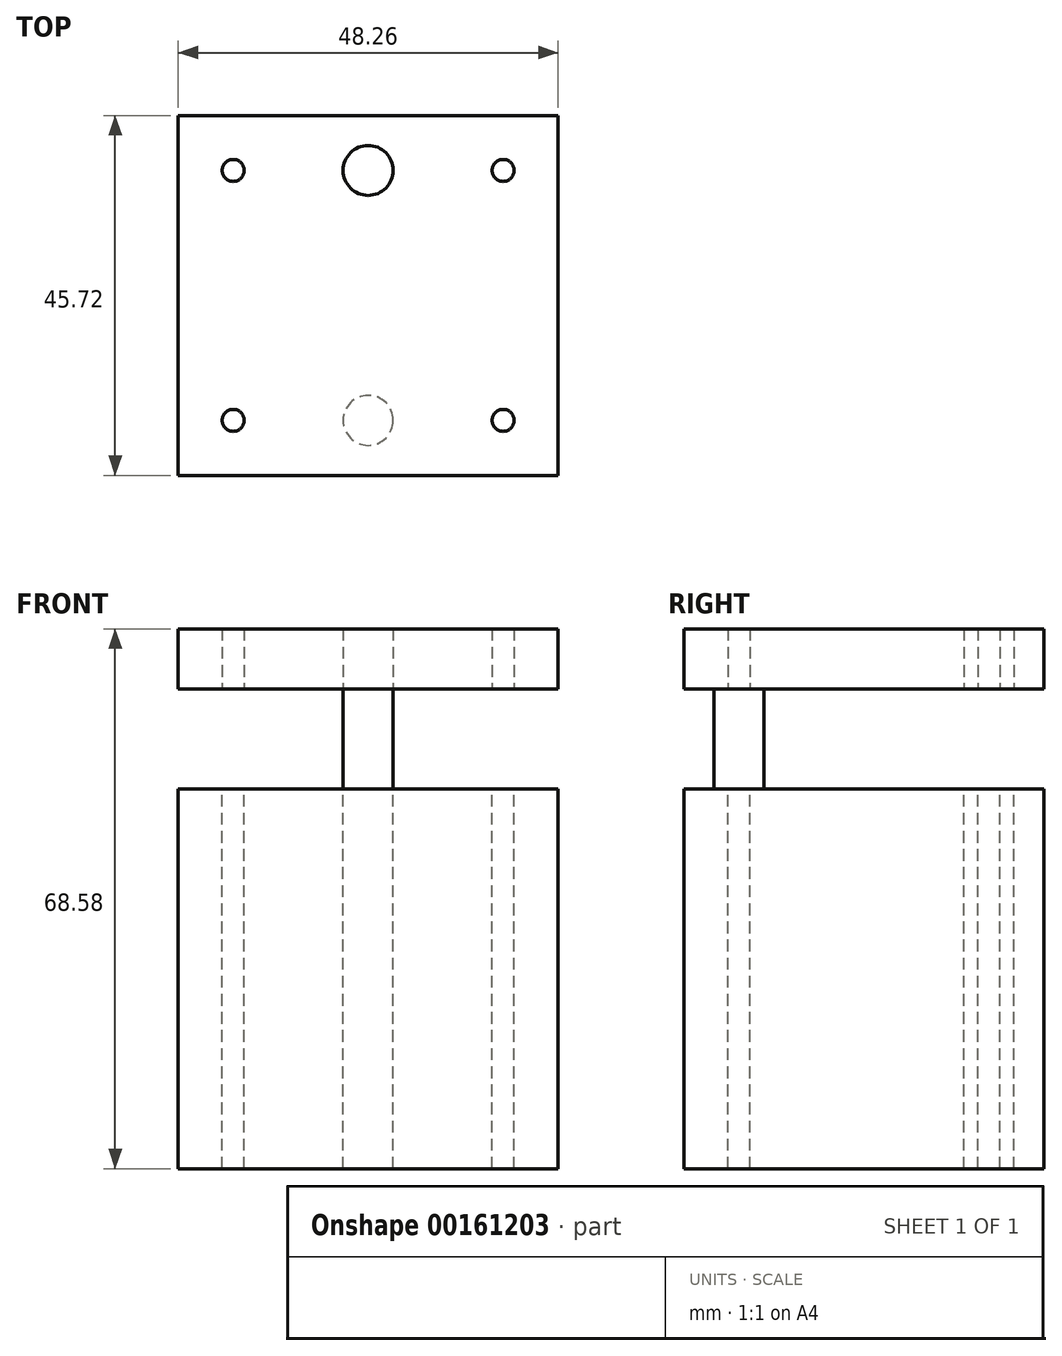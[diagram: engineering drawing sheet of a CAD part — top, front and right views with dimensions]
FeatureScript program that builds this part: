
annotation { "Feature Type Name" : "Feature", "Feature Type Description" : "" }
export const myFeature = defineFeature(function(context is Context, id is Id, definition is map)
    precondition{}
    {
        {
            var Q0;
            Q0=qCreatedBy(makeId("Top.planeOp"),FACE);
            var sketch = newSketch(context, id + "F0", { "sketchPlane" : qUnion([Q0])});
            skLineSegment(sketch, "E0.bottom", {"start": v(24.13, 22.86) * mm, "end": v(-24.13, 22.86) * mm});
            skLineSegment(sketch, "E0.top", {"start": v(24.13, -22.86) * mm, "end": v(-24.13, -22.86) * mm});
            skLineSegment(sketch, "E0.left", {"start": v(24.13, 22.86) * mm, "end": v(24.13, -22.86) * mm});
            skLineSegment(sketch, "E0.right", {"start": v(-24.13, 22.86) * mm, "end": v(-24.13, -22.86) * mm});
            skPoint(sketch, "E0.middle", {"position": v(0, 0) * mm});
            skCircle(sketch, "E1", {"center": v(17.14, -15.87) * mm, "radius": 1.4 * mm});
            skCircle(sketch, "E2.MirrorC", {"center": v(-17.14, -15.87) * mm, "radius": 1.4 * mm});
            skCircle(sketch, "E3.MirrorC", {"center": v(-17.14, 15.87) * mm, "radius": 1.4 * mm});
            skCircle(sketch, "E4.MirrorC", {"center": v(17.14, 15.87) * mm, "radius": 1.4 * mm});
            skCircle(sketch, "E5", {"center": v(0, -15.88) * mm, "radius": 3.18 * mm});
            skCircle(sketch, "E6.MirrorC", {"center": v(0, 15.88) * mm, "radius": 3.18 * mm});
            skSolve(sketch);
        }
        {
            var Q0;
            Q0=makeQuery(id+"F0.imprint","IMPRINT",FACE,{"disambiguationData":[TD([[makeQuery(id+"F0.imprint","IMPRINT",EDGE,{"derivedFrom":sQuery(id+"F0.wireOp",EDGE,"E3.MirrorC")}),1.0]])]});
            var Q1;
            Q1=makeQuery(id+"F0.imprint","IMPRINT",FACE,{"disambiguationData":[TD([[makeQuery(id+"F0.imprint","IMPRINT",EDGE,{"derivedFrom":sQuery(id+"F0.wireOp",EDGE,"E2.MirrorC")}),-1.0]])]});
            var Q2;
            Q2=makeQuery(id+"F0.imprint","IMPRINT",FACE,{"disambiguationData":[TD([[makeQuery(id+"F0.imprint","IMPRINT",EDGE,{"derivedFrom":sQuery(id+"F0.wireOp",EDGE,"E6.MirrorC")}),-1.0]])]});
            var Q3;
            Q3=makeQuery(id+"F0.imprint","IMPRINT",FACE,{"disambiguationData":[TD([[makeQuery(id+"F0.imprint","IMPRINT",EDGE,{"derivedFrom":sQuery(id+"F0.wireOp",EDGE,"E5")}),1.0]])]});
            var Q4;
            Q4=makeQuery(id+"F0.imprint","IMPRINT",FACE,{"disambiguationData":[TD([[makeQuery(id+"F0.imprint","IMPRINT",EDGE,{"derivedFrom":sQuery(id+"F0.wireOp",EDGE,"E4.MirrorC")}),-1.0]])]});
            var Q5;
            Q5=makeQuery(id+"F0.imprint","IMPRINT",FACE,{"disambiguationData":[TD([[makeQuery(id+"F0.imprint","IMPRINT",EDGE,{"derivedFrom":sQuery(id+"F0.wireOp",EDGE,"E1")}),1.0]])]});
            var Q6;
            Q6=makeQuery(id+"F0.imprint","IMPRINT",FACE,{"disambiguationData":[TD([[makeQuery(id+"F0.imprint","IMPRINT",EDGE,{"derivedFrom":sQuery(id+"F0.wireOp",EDGE,"E0.bottom")}),1.0]])]});
            extrude(context, id + "F1", {"entities" : qUnion([Q0, Q1, Q2, Q3, Q4, Q5, Q6]), "oppositeDirection" : true, "depth" : 60.96 * mm});
        }
        {
            var Q0;
            Q0=makeQuery(id+"F0.imprint","IMPRINT",FACE,{"disambiguationData":[TD([[makeQuery(id+"F0.imprint","IMPRINT",EDGE,{"derivedFrom":sQuery(id+"F0.wireOp",EDGE,"E3.MirrorC")}),1.0]])]});
            var Q1;
            Q1=makeQuery(id+"F0.imprint","IMPRINT",FACE,{"disambiguationData":[TD([[makeQuery(id+"F0.imprint","IMPRINT",EDGE,{"derivedFrom":sQuery(id+"F0.wireOp",EDGE,"E2.MirrorC")}),-1.0]])]});
            var Q2;
            Q2=makeQuery(id+"F0.imprint","IMPRINT",FACE,{"disambiguationData":[TD([[makeQuery(id+"F0.imprint","IMPRINT",EDGE,{"derivedFrom":sQuery(id+"F0.wireOp",EDGE,"E4.MirrorC")}),-1.0]])]});
            var Q3;
            Q3=makeQuery(id+"F0.imprint","IMPRINT",FACE,{"disambiguationData":[TD([[makeQuery(id+"F0.imprint","IMPRINT",EDGE,{"derivedFrom":sQuery(id+"F0.wireOp",EDGE,"E1")}),1.0]])]});
            extrude(context, id + "F2", {"entities" : qUnion([Q0, Q1, Q2, Q3]), "operationType" : NewBodyOperationType.REMOVE, "oppositeDirection" : true, "depth" : 12.7 * mm});
        }
        {
            var Q0;
            Q0=makeQuery(id+"F0.imprint","IMPRINT",FACE,{"disambiguationData":[TD([[makeQuery(id+"F0.imprint","IMPRINT",EDGE,{"derivedFrom":sQuery(id+"F0.wireOp",EDGE,"E6.MirrorC")}),-1.0]])]});
            var Q1;
            Q1=makeQuery(id+"F0.imprint","IMPRINT",FACE,{"disambiguationData":[TD([[makeQuery(id+"F0.imprint","IMPRINT",EDGE,{"derivedFrom":sQuery(id+"F0.wireOp",EDGE,"E5")}),1.0]])]});
            extrude(context, id + "F3", {"entities" : qUnion([Q0, Q1]), "operationType" : NewBodyOperationType.ADD, "depth" : 7.62 * mm});
        }
    });
